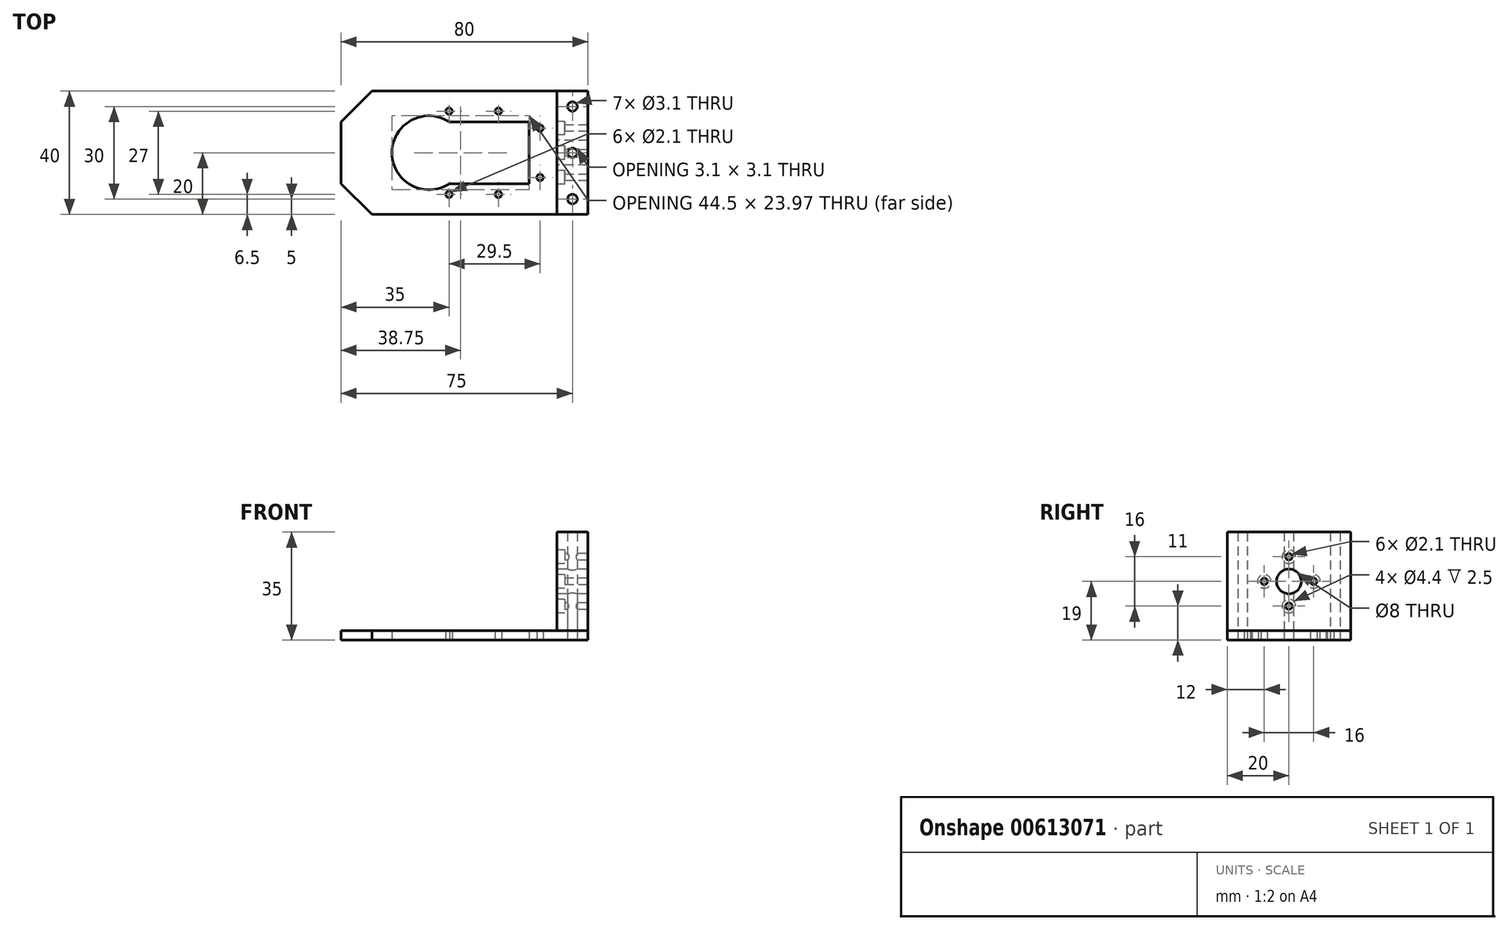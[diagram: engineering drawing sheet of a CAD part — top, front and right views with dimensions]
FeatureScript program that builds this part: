
annotation { "Feature Type Name" : "Feature", "Feature Type Description" : "" }
export const myFeature = defineFeature(function(context is Context, id is Id, definition is map)
    precondition{}
    {
        {
            var Q0;
            Q0=qCreatedBy(makeId("Top.planeOp"),FACE);
            var sketch = newSketch(context, id + "F0", { "sketchPlane" : qUnion([Q0])});
            skCircle(sketch, "E0", {"center": v(0, 0) * mm, "radius": 12 * mm});
            skLineSegment(sketch, "E1", {"start": v(6.63, 10) * mm, "end": v(32.5, 10) * mm});
            skLineSegment(sketch, "E2", {"start": v(32.5, 10) * mm, "end": v(32.5, -10) * mm});
            skLineSegment(sketch, "E3", {"start": v(32.5, -10) * mm, "end": v(6.63, -10) * mm});
            skLineSegment(sketch, "E4", {"start": v(0, 0) * mm, "end": v(32.5, 0) * mm, "construction": true});
            skPoint(sketch, "E5", {"position": v(6.5, 13.5) * mm});
            skPoint(sketch, "E6", {"position": v(22.5, 13.5) * mm});
            skPoint(sketch, "E7", {"position": v(6.5, -13.5) * mm});
            skPoint(sketch, "E8", {"position": v(22.5, -13.5) * mm});
            skPoint(sketch, "E9", {"position": v(36, -8) * mm});
            skPoint(sketch, "E10", {"position": v(36, 8) * mm});
            skLineSegment(sketch, "E11", {"start": v(51.5, 20) * mm, "end": v(51.5, -20) * mm});
            skLineSegment(sketch, "E12", {"start": v(51.5, -20) * mm, "end": v(-18.5, -20) * mm});
            skLineSegment(sketch, "E13", {"start": v(-18.5, -20) * mm, "end": v(-28.5, -10) * mm});
            skLineSegment(sketch, "E14", {"start": v(-28.5, -10) * mm, "end": v(-28.5, 10) * mm});
            skLineSegment(sketch, "E15", {"start": v(-28.5, 10) * mm, "end": v(-18.5, 20) * mm});
            skLineSegment(sketch, "E16", {"start": v(-18.5, 20) * mm, "end": v(51.5, 20) * mm});
            skCircle(sketch, "E17", {"center": v(6.5, 13.5) * mm, "radius": 1.05 * mm});
            skCircle(sketch, "E18", {"center": v(22.5, 13.5) * mm, "radius": 1.05 * mm});
            skCircle(sketch, "E19", {"center": v(36, 8) * mm, "radius": 1.05 * mm});
            skCircle(sketch, "E20", {"center": v(36, -8) * mm, "radius": 1.05 * mm});
            skCircle(sketch, "E21", {"center": v(22.5, -13.5) * mm, "radius": 1.05 * mm});
            skCircle(sketch, "E22", {"center": v(6.5, -13.5) * mm, "radius": 1.05 * mm});
            skCircle(sketch, "E23", {"center": v(46.5, 15) * mm, "radius": 1.55 * mm});
            skLineSegment(sketch, "E24", {"start": v(51.5, 0) * mm, "end": v(44.08, 0) * mm, "construction": true});
            skPoint(sketch, "E24.endSnap0", {"position": v(51.5, 0) * mm});
            skCircle(sketch, "E25", {"center": v(46.5, 0) * mm, "radius": 1.55 * mm});
            skCircle(sketch, "E26", {"center": v(46.5, -15) * mm, "radius": 1.55 * mm});
            skSolve(sketch);
        }
        {
            var Q0;
            {var subQ0=sQuery(id+"F0.wireOp",EDGE,"E1");Q0=makeQuery(id+"F0.imprint","IMPRINT",FACE,{"disambiguationData":[TD([[makeQuery(id+"F0.imprint","IMPRINT",EDGE,{"derivedFrom":subQ0}),1.0]])]});}
            extrude(context, id + "F1", {"entities" : qUnion([Q0]), "depth" : 3 * mm, "offsetDistance" : 25 * mm});
        }
        {
            var Q0;
            Q0=makeQuery(id+"F1.opExtrude","CAP_FACE",FACE,{"disambiguationData":[OSD([sQuery(id+"F0.wireOp",EDGE,"E0"),sQuery(id+"F0.wireOp",EDGE,"E1"),sQuery(id+"F0.wireOp",EDGE,"E2"),sQuery(id+"F0.wireOp",EDGE,"E3"),sQuery(id+"F0.wireOp",EDGE,"E11"),sQuery(id+"F0.wireOp",EDGE,"E12"),sQuery(id+"F0.wireOp",EDGE,"E13"),sQuery(id+"F0.wireOp",EDGE,"E14"),sQuery(id+"F0.wireOp",EDGE,"E15"),sQuery(id+"F0.wireOp",EDGE,"E16"),sQuery(id+"F0.wireOp",EDGE,"E17"),sQuery(id+"F0.wireOp",EDGE,"E18"),sQuery(id+"F0.wireOp",EDGE,"E19"),sQuery(id+"F0.wireOp",EDGE,"E20"),sQuery(id+"F0.wireOp",EDGE,"E21"),sQuery(id+"F0.wireOp",EDGE,"E22"),sQuery(id+"F0.wireOp",EDGE,"E23"),sQuery(id+"F0.wireOp",EDGE,"E25"),sQuery(id+"F0.wireOp",EDGE,"E26")])],"isStart":false});
            var sketch = newSketch(context, id + "F2", { "sketchPlane" : qUnion([Q0])});
            skLineSegment(sketch, "E27", {"start": v(41.5, -20) * mm, "end": v(41.5, 20) * mm});
            skSolve(sketch);
        }
        {
            var Q0;
            {var subQ1=sQuery(id+"F2.wireOp",EDGE,"E27");Q0=makeQuery(id+"F2.imprint","IMPRINT",FACE,{"disambiguationData":[TD([[makeQuery(id+"F2.imprint","IMPRINT",EDGE,{"derivedFrom":subQ1}),-1.0]])]});}
            extrude(context, id + "F3", {"entities" : qUnion([Q0]), "depth" : 32 * mm, "offsetDistance" : 25 * mm});
        }
        {
            var Q0;
            Q0=makeQuery(id+"F3.opExtrude","SWEPT_FACE",FACE,{"disambiguationData":[OSD([sQuery(id+"F2.wireOp",EDGE,"E27")])]});
            var sketch = newSketch(context, id + "F4", { "sketchPlane" : qUnion([Q0])});
            skCircle(sketch, "E28", {"center": v(0, 19) * mm, "radius": 8 * mm, "construction": true});
            skPoint(sketch, "E28.centerSnap0", {"position": v(-20, 19) * mm});
            skPoint(sketch, "E28.centerSnap1", {"position": v(0, 35) * mm});
            skCircle(sketch, "E29", {"center": v(0, 19) * mm, "radius": 4 * mm});
            skPoint(sketch, "E30", {"position": v(0, 27) * mm});
            skPoint(sketch, "E31", {"position": v(0, 11) * mm});
            skPoint(sketch, "E32", {"position": v(-8, 19) * mm});
            skPoint(sketch, "E33", {"position": v(8, 19) * mm});
            skSolve(sketch);
        }
        {
            var Q0;
            Q0=makeQuery(id+"F4.imprint","IMPRINT",FACE,{"disambiguationData":[TD([[makeQuery(id+"F4.imprint","IMPRINT",EDGE,{"derivedFrom":sQuery(id+"F4.wireOp",EDGE,"E29")}),1.0]])]});
            extrude(context, id + "F5", {"entities" : qUnion([Q0]), "operationType" : NewBodyOperationType.REMOVE, "oppositeDirection" : true, "depth" : 25 * mm, "offsetDistance" : 25 * mm});
        }
        {
            var Q0;
            Q0=sQuery(id+"F4.wireOp",VERTEX,"E30");
            var Q1;
            Q1=sQuery(id+"F4.wireOp",VERTEX,"E33");
            var Q2;
            Q2=sQuery(id+"F4.wireOp",VERTEX,"E31");
            var Q3;
            Q3=sQuery(id+"F4.wireOp",VERTEX,"E32");
            var Q4;
            Q4=makeQuery(id+"F3.opExtrude","SWEPT_BODY",BODY,{"disambiguationData":[OSD([sQuery(id+"F0.wireOp",EDGE,"E11"),sQuery(id+"F0.wireOp",EDGE,"E12"),sQuery(id+"F0.wireOp",EDGE,"E16"),sQuery(id+"F0.wireOp",EDGE,"E23"),sQuery(id+"F0.wireOp",EDGE,"E25"),sQuery(id+"F0.wireOp",EDGE,"E26"),sQuery(id+"F2.wireOp",EDGE,"E27")])]});
            hole(context, id + "F6", {"style" : HoleStyle.C_BORE, "endStyle" : HoleEndStyle.THROUGH, "holeDiameter" : 2.1 * mm, "cBoreDiameter" : 4.4 * mm, "cBoreDepth" : 2.5 * mm, "majorDiameter" : 5 * mm, "isTappedThrough" : true, "tappedDepth" : 12 * mm, "tapClearance" : 3, "locations" : qUnion([Q0, Q1, Q2, Q3]), "scope" : qUnion([Q4])});
        }
    });
